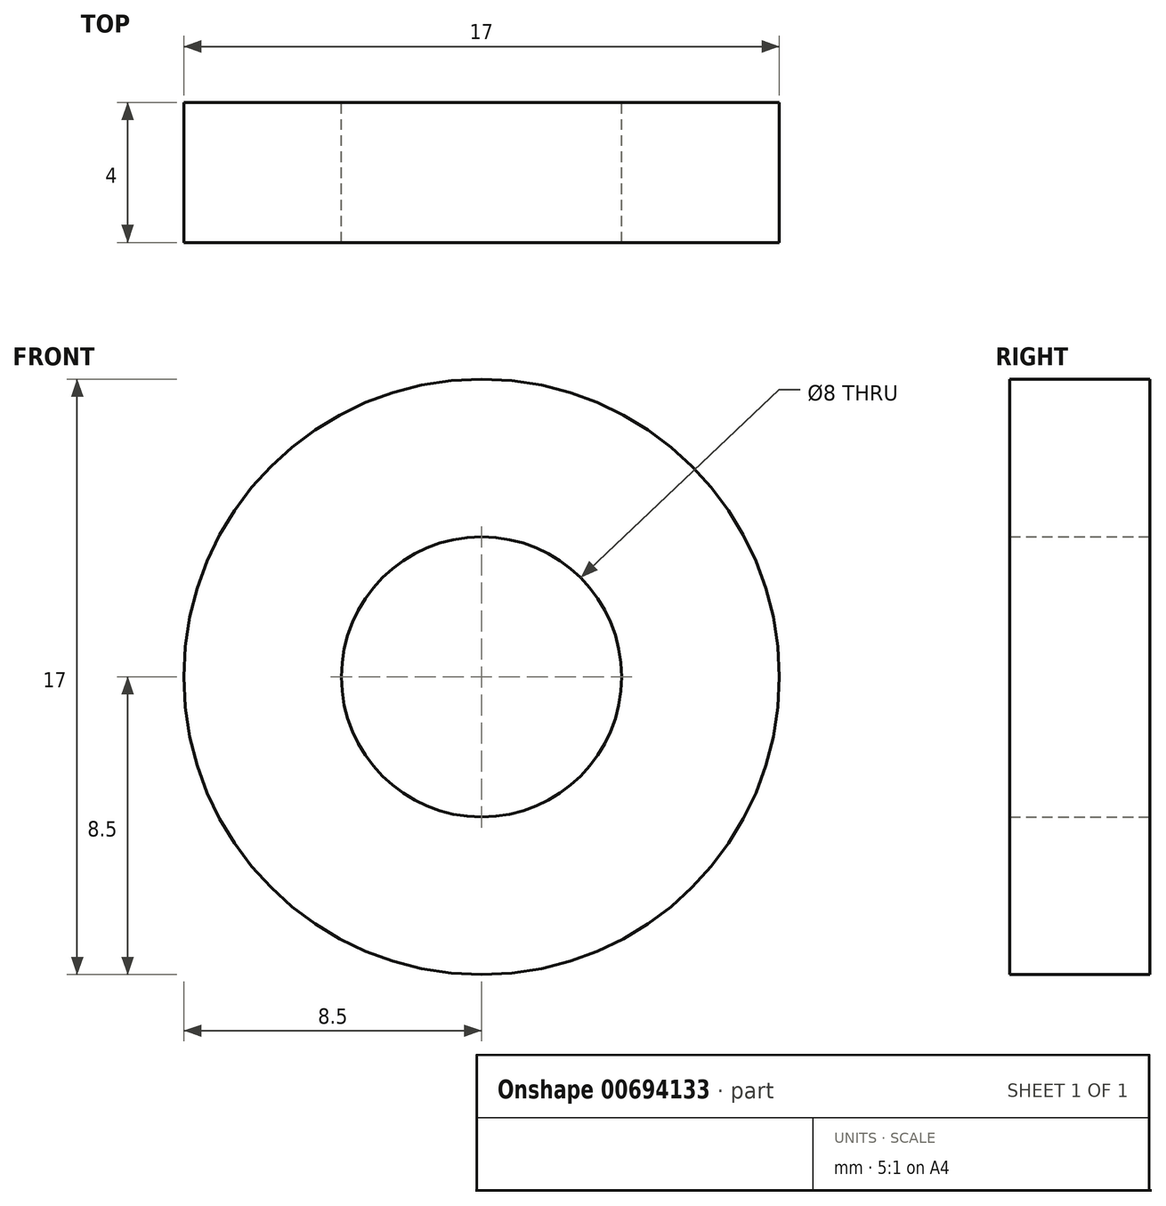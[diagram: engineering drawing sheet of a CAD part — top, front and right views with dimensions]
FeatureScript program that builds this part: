
annotation { "Feature Type Name" : "Feature", "Feature Type Description" : "" }
export const myFeature = defineFeature(function(context is Context, id is Id, definition is map)
    precondition{}
    {
        {
            var Q0;
            Q0=qCreatedBy(makeId("Front.planeOp"),FACE);
            var sketch = newSketch(context, id + "F0", { "sketchPlane" : qUnion([Q0])});
            skCircle(sketch, "E0", {"center": v(0, 0) * mm, "radius": 4 * mm});
            skCircle(sketch, "E1", {"center": v(0, 0) * mm, "radius": 8.5 * mm});
            skSolve(sketch);
        }
        {
            var Q0;
            Q0=makeQuery(id+"F0.imprint","IMPRINT",FACE,{"disambiguationData":[TD([[makeQuery(id+"F0.imprint","IMPRINT",EDGE,{"derivedFrom":sQuery(id+"F0.wireOp",EDGE,"E0")}),-1.0]])]});
            extrude(context, id + "F1", {"entities" : qUnion([Q0]), "depth" : 4 * mm, "offsetDistance" : 25 * mm});
        }
    });
